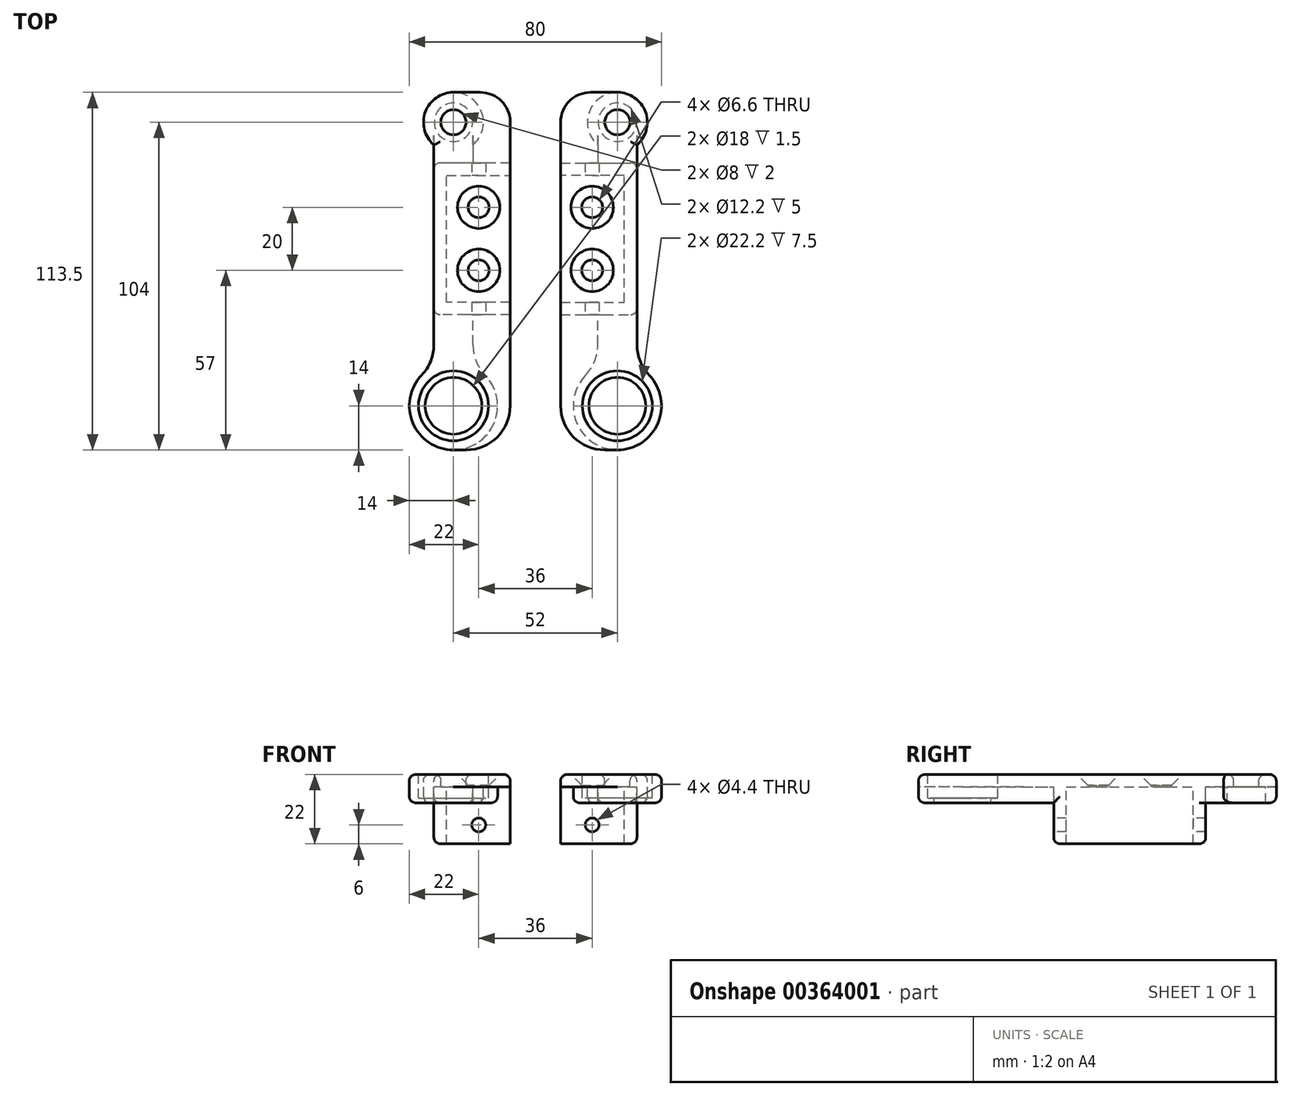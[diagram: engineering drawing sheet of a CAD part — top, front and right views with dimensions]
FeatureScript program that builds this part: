
annotation { "Feature Type Name" : "Feature", "Feature Type Description" : "" }
export const myFeature = defineFeature(function(context is Context, id is Id, definition is map)
    precondition{}
    {
        {
            var Q0;
            Q0=qCreatedBy(makeId("Top.planeOp"),FACE);
            var sketch = newSketch(context, id + "F0", { "sketchPlane" : qUnion([Q0])});
            skArc(sketch, "E0", {"start": v(26, 46.5) * mm, "mid": v(34.9, 40.3) * mm, "end": v(32.2, 29.8) * mm});
            skArc(sketch, "E1", {"start": v(36.1, -43.3) * mm, "mid": v(38.88, -58.49) * mm, "end": v(26, -67) * mm});
            skArc(sketch, "E2", {"start": v(36.1, -43.3) * mm, "mid": v(33.21, -38.84) * mm, "end": v(32.2, -33.61) * mm});
            skLineSegment(sketch, "E3", {"start": v(32.2, -33.61) * mm, "end": v(32.2, 29.8) * mm});
            skLineSegment(sketch, "E4", {"start": v(8, -53) * mm, "end": v(8, 37) * mm});
            skArc(sketch, "E5", {"start": v(8, -53) * mm, "mid": v(12.1, -62.9) * mm, "end": v(22, -67) * mm});
            skLineSegment(sketch, "E6", {"start": v(22, -67) * mm, "end": v(26, -67) * mm});
            skArc(sketch, "E7", {"start": v(8, 37) * mm, "mid": v(10.78, 43.72) * mm, "end": v(17.5, 46.5) * mm});
            skLineSegment(sketch, "E8", {"start": v(17.5, 46.5) * mm, "end": v(26, 46.5) * mm});
            skCircle(sketch, "E9", {"center": v(26, 37) * mm, "radius": 4 * mm});
            skCircle(sketch, "E10", {"center": v(26, -53) * mm, "radius": 9 * mm});
            skSolve(sketch);
        }
        {
            var Q0;
            Q0 = qSketchRegion(id + "F0", true);
            extrude(context, id + "F1", {"entities" : qUnion([Q0]), "oppositeDirection" : true, "depth" : 4 * mm});
        }
        {
            var Q0;
            Q0=makeQuery(id+"F1.opExtrude","CAP_FACE",FACE,{"disambiguationData":[OSD([sQuery(id+"F0.wireOp",EDGE,"E0"),sQuery(id+"F0.wireOp",EDGE,"E1"),sQuery(id+"F0.wireOp",EDGE,"E2"),sQuery(id+"F0.wireOp",EDGE,"E3"),sQuery(id+"F0.wireOp",EDGE,"E4"),sQuery(id+"F0.wireOp",EDGE,"E5"),sQuery(id+"F0.wireOp",EDGE,"E6"),sQuery(id+"F0.wireOp",EDGE,"E7"),sQuery(id+"F0.wireOp",EDGE,"E8")])],"isStart":true});
            var sketch = newSketch(context, id + "F2", { "sketchPlane" : qUnion([Q0])});
            skPoint(sketch, "E11", {"position": v(18, 10) * mm});
            skPoint(sketch, "E12", {"position": v(18, -10) * mm});
            skSolve(sketch);
        }
        {
            var Q0;
            Q0=sQuery(id+"F2.wireOp",VERTEX,"E11");
            var Q1;
            Q1=sQuery(id+"F2.wireOp",VERTEX,"E12");
            var Q2;
            Q2=makeQuery(id+"F1.opExtrude","SWEPT_BODY",BODY,{"disambiguationData":[OSD([sQuery(id+"F0.wireOp",EDGE,"E0"),sQuery(id+"F0.wireOp",EDGE,"E1"),sQuery(id+"F0.wireOp",EDGE,"E2"),sQuery(id+"F0.wireOp",EDGE,"E3"),sQuery(id+"F0.wireOp",EDGE,"E4"),sQuery(id+"F0.wireOp",EDGE,"E5"),sQuery(id+"F0.wireOp",EDGE,"E6"),sQuery(id+"F0.wireOp",EDGE,"E7"),sQuery(id+"F0.wireOp",EDGE,"E8")])]});
            hole(context, id + "F3", {"style" : HoleStyle.C_SINK, "endStyle" : HoleEndStyle.THROUGH, "standardTappedOrClearance" : lookupTablePath({ "standard" : "ISO", "fit" : "Normal", "size" : "M6", "type" : "Clearance" }), "standardBlindInLast" : lookupTablePath({ "fit" : "Standard", "standard" : "ISO", "size" : "M6", "type" : "Clearance" }), "holeDiameter" : 6.6 * mm, "cSinkDiameter" : 13.44 * mm, "cSinkAngle" : 90 * degree, "isTappedThrough" : true, "tappedDepth" : 12 * mm, "tapClearance" : 3, "locations" : qUnion([Q0, Q1]), "scope" : qUnion([Q2]), "startStyle" : HoleStartStyle.PART});
        }
        {
            var Q0;
            Q0=makeQuery(id+"F1.opExtrude","CAP_FACE",FACE,{"disambiguationData":[OSD([sQuery(id+"F0.wireOp",EDGE,"E0"),sQuery(id+"F0.wireOp",EDGE,"E1"),sQuery(id+"F0.wireOp",EDGE,"E2"),sQuery(id+"F0.wireOp",EDGE,"E3"),sQuery(id+"F0.wireOp",EDGE,"E4"),sQuery(id+"F0.wireOp",EDGE,"E5"),sQuery(id+"F0.wireOp",EDGE,"E6"),sQuery(id+"F0.wireOp",EDGE,"E7"),sQuery(id+"F0.wireOp",EDGE,"E8")])],"isStart":false});
            var sketch = newSketch(context, id + "F4", { "sketchPlane" : qUnion([Q0])});
            skLineSegment(sketch, "E13", {"start": v(8, 20.1) * mm, "end": v(28.2, 20.1) * mm});
            skLineSegment(sketch, "E14", {"start": v(28.2, 20.1) * mm, "end": v(28.2, -20.1) * mm});
            skLineSegment(sketch, "E15", {"start": v(28.2, -20.1) * mm, "end": v(8, -20.1) * mm});
            skLineSegment(sketch, "E16", {"start": v(8, -20.1) * mm, "end": v(8, -24.1) * mm});
            skLineSegment(sketch, "E17", {"start": v(32.2, 24.1) * mm, "end": v(32.2, -24.1) * mm});
            skLineSegment(sketch, "E18", {"start": v(8, 24.1) * mm, "end": v(32.2, 24.1) * mm});
            skLineSegment(sketch, "E19", {"start": v(8, -24.1) * mm, "end": v(32.2, -24.1) * mm});
            skLineSegment(sketch, "E20", {"start": v(8, 20.1) * mm, "end": v(8, 24.1) * mm});
            skSolve(sketch);
        }
        {
            var Q0;
            Q0 = qSketchRegion(id + "F4", true);
            extrude(context, id + "F5", {"entities" : qUnion([Q0]), "operationType" : NewBodyOperationType.ADD, "depth" : 18 * mm});
        }
        {
            var Q0;
            {var subQ0=sQuery(id+"F0.wireOp",EDGE,"E8");var subQ1=sQuery(id+"F0.wireOp",EDGE,"E0");var subQ2=sQuery(id+"F0.wireOp",EDGE,"E3");var subQ3=sQuery(id+"F0.wireOp",EDGE,"E7");var subQ4=sQuery(id+"F0.wireOp",EDGE,"E4");Q0=makeQuery(id+"F5.boolean.opBoolean","SPLIT",FACE,{"disambiguationData":[TD([makeQuery(id+"F1.opExtrude","SWEPT_FACE",FACE,{"disambiguationData":[OSD([subQ1])]})])],"derivedFrom":makeQuery(id+"F1.opExtrude","CAP_FACE",FACE,{"disambiguationData":[OSD([subQ1,sQuery(id+"F0.wireOp",EDGE,"E1"),sQuery(id+"F0.wireOp",EDGE,"E2"),subQ2,subQ4,sQuery(id+"F0.wireOp",EDGE,"E5"),sQuery(id+"F0.wireOp",EDGE,"E6"),subQ3,subQ0])],"isStart":false})});}
            var sketch = newSketch(context, id + "F6", { "sketchPlane" : qUnion([Q0])});
            skLineSegment(sketch, "E21", {"start": v(32.2, -24.1) * mm, "end": v(32.2, -29.8) * mm});
            skArc(sketch, "E22", {"start": v(19.8, -29.8) * mm, "mid": v(26, -46.5) * mm, "end": v(32.2, -29.8) * mm});
            skCircle(sketch, "E23", {"center": v(26, -37) * mm, "radius": 6.1 * mm});
            skLineSegment(sketch, "E24", {"start": v(19.8, -29.8) * mm, "end": v(19.8, -24.1) * mm});
            skLineSegment(sketch, "E25", {"start": v(19.8, -24.1) * mm, "end": v(32.2, -24.1) * mm});
            skSolve(sketch);
        }
        {
            var Q0;
            Q0 = qSketchRegion(id + "F6", true);
            extrude(context, id + "F7", {"entities" : qUnion([Q0]), "operationType" : NewBodyOperationType.ADD, "depth" : 5 * mm});
        }
        {
            var Q0;
            Q0=makeQuery(id+"F5.opExtrude","SWEPT_FACE",FACE,{"disambiguationData":[OSD([sQuery(id+"F4.wireOp",EDGE,"E19")])]});
            var sketch = newSketch(context, id + "F8", { "sketchPlane" : qUnion([Q0])});
            skPoint(sketch, "E26", {"position": v(-18, -16) * mm});
            skSolve(sketch);
        }
        {
            var Q0;
            Q0=sQuery(id+"F8.wireOp",VERTEX,"E26");
            var Q1;
            Q1=makeQuery(id+"F1.opExtrude","SWEPT_BODY",BODY,{"disambiguationData":[OSD([sQuery(id+"F0.wireOp",EDGE,"E0"),sQuery(id+"F0.wireOp",EDGE,"E1"),sQuery(id+"F0.wireOp",EDGE,"E2"),sQuery(id+"F0.wireOp",EDGE,"E3"),sQuery(id+"F0.wireOp",EDGE,"E4"),sQuery(id+"F0.wireOp",EDGE,"E5"),sQuery(id+"F0.wireOp",EDGE,"E6"),sQuery(id+"F0.wireOp",EDGE,"E7"),sQuery(id+"F0.wireOp",EDGE,"E8"),sQuery(id+"F0.wireOp",EDGE,"E9"),sQuery(id+"F0.wireOp",EDGE,"E10")])]});
            hole(context, id + "F9", {"style" : HoleStyle.SIMPLE, "endStyle" : HoleEndStyle.THROUGH, "standardTappedOrClearance" : lookupTablePath({ "standard" : "ISO", "fit" : "Normal", "size" : "M4", "type" : "Clearance" }), "standardBlindInLast" : lookupTablePath({ "fit" : "Standard", "standard" : "ISO", "size" : "M4", "type" : "Clearance" }), "holeDiameter" : 4.4 * mm, "isTappedThrough" : true, "tappedDepth" : 12 * mm, "tapClearance" : 3, "locations" : qUnion([Q0]), "scope" : qUnion([Q1]), "startStyle" : HoleStartStyle.PART});
        }
        {
            var Q0;
            {var subQ0=sQuery(id+"F0.wireOp",EDGE,"E1");var subQ1=sQuery(id+"F0.wireOp",EDGE,"E2");var subQ2=sQuery(id+"F0.wireOp",EDGE,"E10");var subQ3=sQuery(id+"F0.wireOp",EDGE,"E6");var subQ4=sQuery(id+"F0.wireOp",EDGE,"E5");var subQ5=sQuery(id+"F0.wireOp",EDGE,"E3");var subQ6=sQuery(id+"F0.wireOp",EDGE,"E4");Q0=makeQuery(id+"F5.boolean.opBoolean","SPLIT",FACE,{"disambiguationData":[TD([makeQuery(id+"F1.opExtrude","SWEPT_FACE",FACE,{"disambiguationData":[OSD([subQ0])]})])],"derivedFrom":makeQuery(id+"F1.opExtrude","CAP_FACE",FACE,{"disambiguationData":[OSD([sQuery(id+"F0.wireOp",EDGE,"E0"),subQ0,subQ1,subQ5,subQ6,subQ4,subQ3,sQuery(id+"F0.wireOp",EDGE,"E7"),sQuery(id+"F0.wireOp",EDGE,"E8"),sQuery(id+"F0.wireOp",EDGE,"E9"),subQ2])],"isStart":false})});}
            var sketch = newSketch(context, id + "F10", { "sketchPlane" : qUnion([Q0])});
            skCircle(sketch, "E27", {"center": v(26, 53) * mm, "radius": 9 * mm});
            skLineSegment(sketch, "E28", {"start": v(32.2, 24.1) * mm, "end": v(32.2, 33.61) * mm});
            skArc(sketch, "E29", {"start": v(36.1, 43.3) * mm, "mid": v(33.21, 38.84) * mm, "end": v(32.2, 33.61) * mm});
            skArc(sketch, "E30", {"start": v(36.1, 43.3) * mm, "mid": v(26, 67) * mm, "end": v(15.9, 43.3) * mm});
            skArc(sketch, "E31", {"start": v(19.8, 33.6) * mm, "mid": v(18.79, 38.84) * mm, "end": v(15.9, 43.3) * mm});
            skLineSegment(sketch, "E32", {"start": v(19.8, 33.6) * mm, "end": v(19.8, 24.1) * mm});
            skLineSegment(sketch, "E33", {"start": v(19.8, 24.1) * mm, "end": v(32.2, 24.1) * mm});
            skSolve(sketch);
        }
        {
            var Q0;
            Q0 = qSketchRegion(id + "F10", true);
            extrude(context, id + "F11", {"entities" : qUnion([Q0]), "operationType" : NewBodyOperationType.ADD, "depth" : 5 * mm});
        }
        {
            var Q0;
            Q0=makeQuery(id+"F1.opExtrude","CAP_FACE",FACE,{"disambiguationData":[OSD([sQuery(id+"F0.wireOp",EDGE,"E0"),sQuery(id+"F0.wireOp",EDGE,"E1"),sQuery(id+"F0.wireOp",EDGE,"E2"),sQuery(id+"F0.wireOp",EDGE,"E3"),sQuery(id+"F0.wireOp",EDGE,"E4"),sQuery(id+"F0.wireOp",EDGE,"E5"),sQuery(id+"F0.wireOp",EDGE,"E6"),sQuery(id+"F0.wireOp",EDGE,"E7"),sQuery(id+"F0.wireOp",EDGE,"E8"),sQuery(id+"F0.wireOp",EDGE,"E9"),sQuery(id+"F0.wireOp",EDGE,"E10")])],"isStart":true});
            var sketch = newSketch(context, id + "F12", { "sketchPlane" : qUnion([Q0])});
            skCircle(sketch, "E34", {"center": v(26, -53) * mm, "radius": 11.1 * mm});
            skSolve(sketch);
        }
        {
            var Q0;
            Q0 = qSketchRegion(id + "F12", true);
            extrude(context, id + "F13", {"entities" : qUnion([Q0]), "operationType" : NewBodyOperationType.REMOVE, "oppositeDirection" : true, "depth" : 7.5 * mm});
        }
        {
            var Q0;
            Q0=makeQuery(id+"F3.hole-1.boolean.opBoolean","COPY",EDGE,{"derivedFrom":makeQuery(id+"F3.hole-1.opRevolve","SWEPT_EDGE",EDGE,{"disambiguationData":[OSD([sQuery(id+"F3.hole-1.sketch.wireOp",EDGE,"csink_start_line_1"),sQuery(id+"F3.hole-1.sketch.wireOp",EDGE,"csink_start_line_2")])]})});
            var Q1;
            Q1=makeQuery(id+"F3.hole-0.boolean.opBoolean","COPY",FACE,{"derivedFrom":makeQuery(id+"F3.hole-0.opRevolve","SWEPT_FACE",FACE,{"disambiguationData":[OSD([sQuery(id+"F3.hole-0.sketch.wireOp",EDGE,"csink_start_line_1")])]})});
            var Q2;
            Q2=makeQuery(id+"F1.opExtrude","CAP_EDGE",EDGE,{"disambiguationData":[OSD([sQuery(id+"F0.wireOp",EDGE,"E9")])],"isStart":true});
            var Q3;
            Q3=makeQuery(id+"F1.opExtrude","CAP_EDGE",EDGE,{"disambiguationData":[OSD([sQuery(id+"F0.wireOp",EDGE,"E7")])],"isStart":true});
            var Q4;
            Q4=makeQuery(id+"F11.opExtrude","CAP_EDGE",EDGE,{"disambiguationData":[OSD([sQuery(id+"F10.wireOp",EDGE,"E32")])],"isStart":false});
            var Q5;
            Q5=makeQuery(id+"F11.opExtrude","CAP_EDGE",EDGE,{"disambiguationData":[OSD([sQuery(id+"F10.wireOp",EDGE,"E32")])],"isStart":true});
            var Q6;
            Q6=makeQuery(id+"F5.opExtrude","CAP_EDGE",EDGE,{"disambiguationData":[OSD([sQuery(id+"F4.wireOp",EDGE,"E18")])],"isStart":true});
            var Q7;
            Q7=makeQuery(id+"F5.opExtrude","CAP_EDGE",EDGE,{"disambiguationData":[OSD([sQuery(id+"F4.wireOp",EDGE,"E18")])],"isStart":false});
            var Q8;
            Q8=makeQuery(id+"F5.opExtrude","SWEPT_EDGE",EDGE,{"disambiguationData":[OSD([sQuery(id+"F0.wireOp",EDGE,"E3"),sQuery(id+"F4.wireOp",EDGE,"E17"),sQuery(id+"F4.wireOp",EDGE,"E18")])]});
            var Q9;
            Q9=makeQuery(id+"F5.opExtrude","CAP_EDGE",EDGE,{"disambiguationData":[OSD([sQuery(id+"F4.wireOp",EDGE,"E17")])],"isStart":false});
            var Q10;
            Q10=makeQuery(id+"F5.opExtrude","CAP_EDGE",EDGE,{"disambiguationData":[OSD([sQuery(id+"F4.wireOp",EDGE,"E19")])],"isStart":false});
            var Q11;
            Q11=makeQuery(id+"F5.opExtrude","SWEPT_EDGE",EDGE,{"disambiguationData":[OSD([sQuery(id+"F0.wireOp",EDGE,"E3"),sQuery(id+"F4.wireOp",EDGE,"E17"),sQuery(id+"F4.wireOp",EDGE,"E19")])]});
            var Q12;
            Q12=makeQuery(id+"F7.opExtrude","CAP_EDGE",EDGE,{"disambiguationData":[OSD([sQuery(id+"F6.wireOp",EDGE,"E22")])],"isStart":false});
            var Q13;
            Q13=makeQuery(id+"F11.opExtrude","CAP_EDGE",EDGE,{"disambiguationData":[OSD([sQuery(id+"F10.wireOp",EDGE,"E33")])],"isStart":false});
            var Q14;
            Q14=makeQuery(id+"F7.opExtrude","CAP_EDGE",EDGE,{"disambiguationData":[OSD([sQuery(id+"F6.wireOp",EDGE,"E25")])],"isStart":false});
            var Q15;
            Q15=makeQuery(id+"F5.opExtrude","CAP_EDGE",EDGE,{"disambiguationData":[OSD([sQuery(id+"F4.wireOp",EDGE,"E19")])],"isStart":true});
            var Q16;
            Q16=makeQuery(id+"F7.opExtrude","SWEPT_EDGE",EDGE,{"disambiguationData":[OSD([sQuery(id+"F4.wireOp",EDGE,"E19"),sQuery(id+"F6.wireOp",EDGE,"E24"),sQuery(id+"F6.wireOp",EDGE,"E25")])]});
            var Q17;
            Q17=makeQuery(id+"F7.opExtrude","CAP_EDGE",EDGE,{"disambiguationData":[OSD([sQuery(id+"F6.wireOp",EDGE,"E22")])],"isStart":true});
            var Q18;
            Q18=makeQuery(id+"F7.opExtrude","CAP_EDGE",EDGE,{"disambiguationData":[OSD([sQuery(id+"F6.wireOp",EDGE,"E24")])],"isStart":true});
            fillet(context, id + "F14", {"entities" : qUnion([Q0, Q1, Q2, Q3, Q4, Q5, Q6, Q7, Q8, Q9, Q10, Q11, Q12, Q13, Q14, Q15, Q16, Q17, Q18]), "radius" : 2 * mm, "tangentPropagation" : true, "allowEdgeOverflow" : false});
        }
        {
            var Q0;
            Q0=makeQuery(id+"F1.opExtrude","SWEPT_BODY",BODY,{"disambiguationData":[OSD([sQuery(id+"F0.wireOp",EDGE,"E0"),sQuery(id+"F0.wireOp",EDGE,"E1"),sQuery(id+"F0.wireOp",EDGE,"E2"),sQuery(id+"F0.wireOp",EDGE,"E3"),sQuery(id+"F0.wireOp",EDGE,"E4"),sQuery(id+"F0.wireOp",EDGE,"E5"),sQuery(id+"F0.wireOp",EDGE,"E6"),sQuery(id+"F0.wireOp",EDGE,"E7"),sQuery(id+"F0.wireOp",EDGE,"E8"),sQuery(id+"F0.wireOp",EDGE,"E9"),sQuery(id+"F0.wireOp",EDGE,"E10")])]});
            var Q1;
            Q1=qCreatedBy(makeId("Right.planeOp"),FACE);
            mirror(context, id + "F15", {"entities" : qUnion([Q0]), "mirrorPlane" : qUnion([Q1])});
        }
    });
